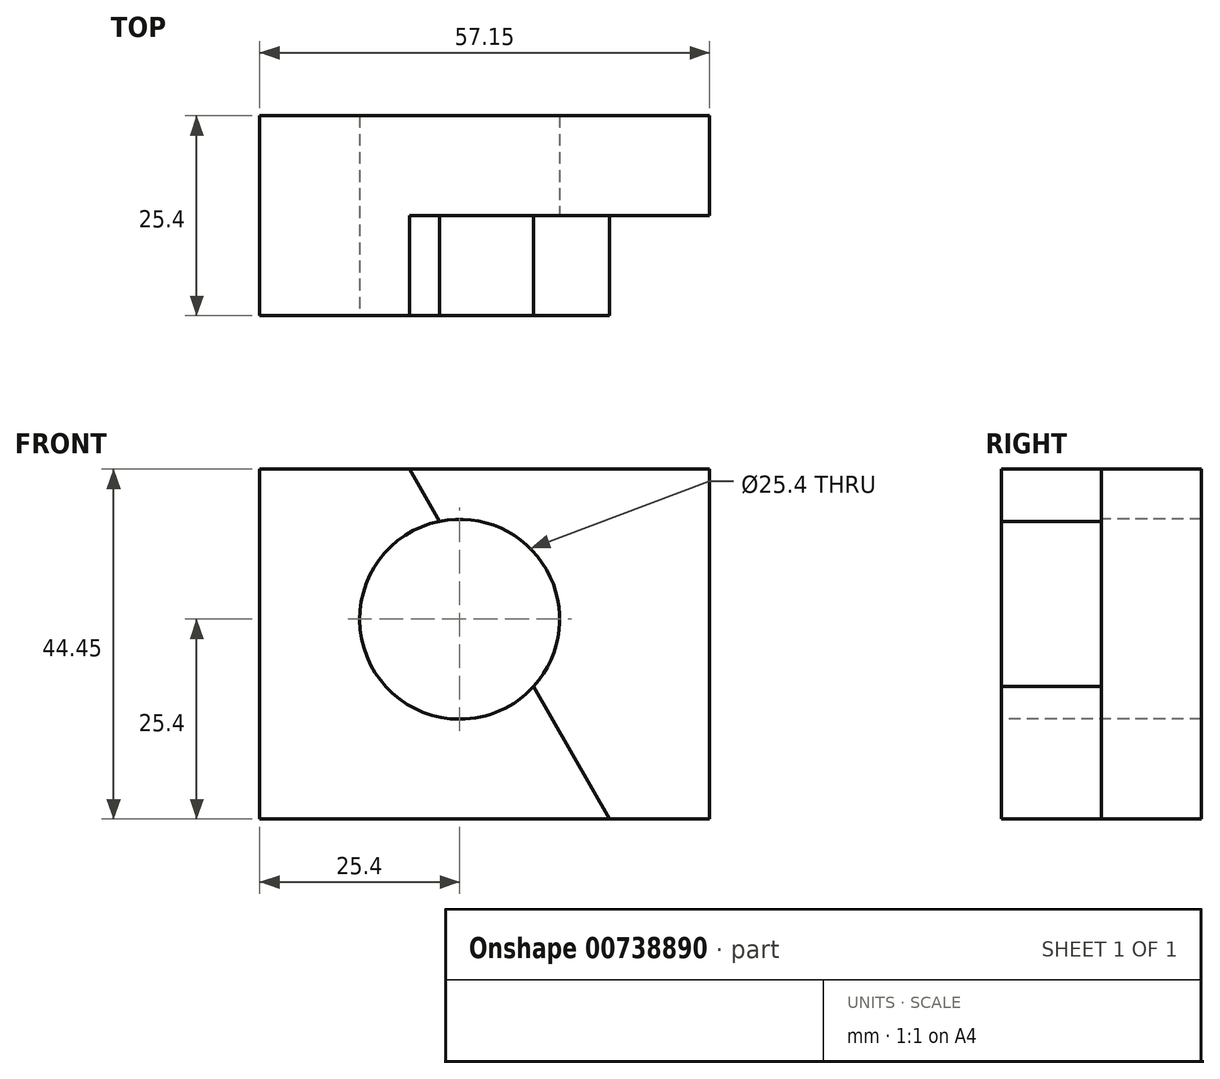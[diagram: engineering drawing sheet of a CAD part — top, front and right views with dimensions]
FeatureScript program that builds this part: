
annotation { "Feature Type Name" : "Feature", "Feature Type Description" : "" }
export const myFeature = defineFeature(function(context is Context, id is Id, definition is map)
    precondition{}
    {
        {
            var Q0;
            Q0=qCreatedBy(makeId("Front.planeOp"),FACE);
            var sketch = newSketch(context, id + "F0", { "sketchPlane" : qUnion([Q0])});
            skLineSegment(sketch, "E0", {"start": v(0, 44.45) * mm, "end": v(0, 0) * mm});
            skLineSegment(sketch, "E1", {"start": v(0, 0) * mm, "end": v(57.15, 0) * mm});
            skLineSegment(sketch, "E2", {"start": v(57.15, 0) * mm, "end": v(57.15, 44.45) * mm});
            skLineSegment(sketch, "E3", {"start": v(57.15, 44.45) * mm, "end": v(0, 44.45) * mm});
            skSolve(sketch);
        }
        {
            var Q0;
            Q0=makeQuery(id+"F0.imprint","IMPRINT",FACE,{"disambiguationData":[TD([[makeQuery(id+"F0.imprint","IMPRINT",EDGE,{"derivedFrom":sQuery(id+"F0.wireOp",EDGE,"E0")}),1.0]])]});
            extrude(context, id + "F1", {"entities" : qUnion([Q0]), "depth" : 25.4 * mm, "offsetDistance" : 25.4 * mm});
        }
        {
            var Q0;
            Q0=makeQuery(id+"F1.opExtrude","CAP_FACE",FACE,{"disambiguationData":[OSD([sQuery(id+"F0.wireOp",EDGE,"E0"),sQuery(id+"F0.wireOp",EDGE,"E1"),sQuery(id+"F0.wireOp",EDGE,"E2"),sQuery(id+"F0.wireOp",EDGE,"E3")])],"isStart":false});
            var sketch = newSketch(context, id + "F2", { "sketchPlane" : qUnion([Q0])});
            skLineSegment(sketch, "E4", {"start": v(0, 38.1) * mm, "end": v(57.15, 38.1) * mm});
            skLineSegment(sketch, "E5", {"start": v(38.1, 44.45) * mm, "end": v(38.1, 0) * mm});
            skLineSegment(sketch, "E6", {"start": v(12.7, 44.45) * mm, "end": v(12.7, 0) * mm});
            skCircle(sketch, "E7", {"center": v(25.4, 25.4) * mm, "radius": 12.7 * mm});
            skSolve(sketch);
        }
        {
            var Q0;
            {var subQ0=sQuery(id+"F2.wireOp",EDGE,"E7");var subQ1=makeQuery(id+"F2.imprint","INTERSECT",VERTEX,{"derivedFrom":[sQuery(id+"F2.wireOp",EDGE,"E4"),subQ0]});Q0=makeQuery(id+"F2.imprint","IMPRINT",FACE,{"disambiguationData":[TD([[makeQuery(id+"F2.imprint","IMPRINT",EDGE,{"disambiguationData":[TD([[subQ1,1.0]])],"derivedFrom":subQ0}),1.0]])]});}
            extrude(context, id + "F3", {"entities" : qUnion([Q0]), "operationType" : NewBodyOperationType.REMOVE, "endBound" : BoundingType.THROUGH_ALL, "oppositeDirection" : true, "depth" : 25.4 * mm, "offsetDistance" : 25.4 * mm});
        }
        {
            var Q0;
            Q0=makeQuery(id+"F1.opExtrude","CAP_FACE",FACE,{"disambiguationData":[OSD([sQuery(id+"F0.wireOp",EDGE,"E0"),sQuery(id+"F0.wireOp",EDGE,"E1"),sQuery(id+"F0.wireOp",EDGE,"E2"),sQuery(id+"F0.wireOp",EDGE,"E3")])],"isStart":false});
            var sketch = newSketch(context, id + "F4", { "sketchPlane" : qUnion([Q0])});
            skLineSegment(sketch, "E8", {"start": v(19.05, 44.45) * mm, "end": v(44.45, 0) * mm});
            skSolve(sketch);
        }
        {
            var Q0;
            Q0 = qSketchRegion(id + "F4", true);
            var Q1;
            {var subQ0=makeQuery(id+"F1.opExtrude","CAP_EDGE",EDGE,{"disambiguationData":[OSD([sQuery(id+"F0.wireOp",EDGE,"E2")])],"isStart":false});Q1=makeQuery(id+"F4.imprint","IMPRINT",FACE,{"disambiguationData":[TD([[makeQuery(id+"F4.imprint","IMPRINT",EDGE,{"derivedFrom":subQ0}),1.0]])]});}
            extrude(context, id + "F5", {"entities" : qUnion([Q0, Q1]), "operationType" : NewBodyOperationType.REMOVE, "oppositeDirection" : true, "depth" : 12.7 * mm, "offsetDistance" : 25.4 * mm});
        }
    });
